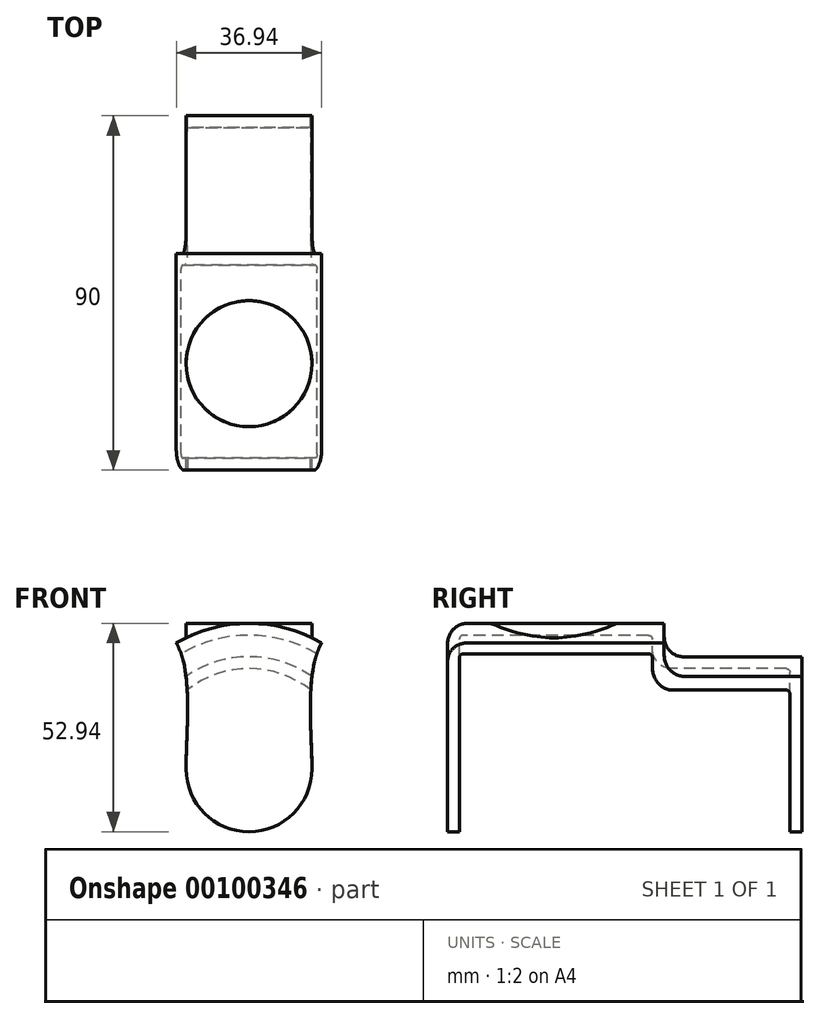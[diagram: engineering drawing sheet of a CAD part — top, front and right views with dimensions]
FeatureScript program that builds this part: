
annotation { "Feature Type Name" : "Feature", "Feature Type Description" : "" }
export const myFeature = defineFeature(function(context is Context, id is Id, definition is map)
    precondition{}
    {
        {
            var Q0;
            Q0=qCreatedBy(makeId("Front.planeOp"),FACE);
            var sketch = newSketch(context, id + "F0", { "sketchPlane" : qUnion([Q0])});
            skLineSegment(sketch, "E0.bottom", {"start": v(24, -24) * mm, "end": v(-24, -24) * mm});
            skLineSegment(sketch, "E0.top", {"start": v(24, 24) * mm, "end": v(-24, 24) * mm});
            skLineSegment(sketch, "E0.left", {"start": v(24, -24) * mm, "end": v(24, 24) * mm});
            skLineSegment(sketch, "E0.right", {"start": v(-24, -24) * mm, "end": v(-24, 24) * mm});
            skPoint(sketch, "E0.middle", {"position": v(0, 0) * mm});
            skLineSegment(sketch, "E1.bottom", {"start": v(18, -18) * mm, "end": v(-18, -18) * mm});
            skLineSegment(sketch, "E1.top", {"start": v(18, 18) * mm, "end": v(-18, 18) * mm});
            skLineSegment(sketch, "E1.left", {"start": v(18, -18) * mm, "end": v(18, 18) * mm});
            skLineSegment(sketch, "E1.right", {"start": v(-18, -18) * mm, "end": v(-18, 18) * mm});
            skLineSegment(sketch, "E2.bottom", {"start": v(18, 36.94) * mm, "end": v(-18, 36.94) * mm});
            skLineSegment(sketch, "E2.top", {"start": v(18, 72.94) * mm, "end": v(-18, 72.94) * mm});
            skLineSegment(sketch, "E2.left", {"start": v(18, 36.94) * mm, "end": v(18, 72.94) * mm});
            skLineSegment(sketch, "E2.right", {"start": v(-18, 36.94) * mm, "end": v(-18, 72.94) * mm});
            skPoint(sketch, "E2.middle", {"position": v(0, 54.94) * mm});
            skLineSegment(sketch, "E3.0", {"start": v(-12, 42.94) * mm, "end": v(-12, 66.94) * mm, "construction": true});
            skLineSegment(sketch, "E3.1", {"start": v(12, 42.94) * mm, "end": v(-12, 42.94) * mm, "construction": true});
            skLineSegment(sketch, "E3.2", {"start": v(12, 42.94) * mm, "end": v(12, 66.94) * mm, "construction": true});
            skLineSegment(sketch, "E3.3", {"start": v(12, 66.94) * mm, "end": v(-12, 66.94) * mm, "construction": true});
            skLineSegment(sketch, "E4.0", {"start": v(12, 12) * mm, "end": v(-12, 12) * mm, "construction": true});
            skLineSegment(sketch, "E4.1", {"start": v(12, -12) * mm, "end": v(12, 12) * mm, "construction": true});
            skLineSegment(sketch, "E4.2", {"start": v(12, -12) * mm, "end": v(-12, -12) * mm, "construction": true});
            skLineSegment(sketch, "E4.3", {"start": v(-12, -12) * mm, "end": v(-12, 12) * mm, "construction": true});
            skLineSegment(sketch, "E5.0", {"start": v(18, 18) * mm, "end": v(-18, 18) * mm, "construction": true});
            skLineSegment(sketch, "E5.1", {"start": v(18, -18) * mm, "end": v(18, 18) * mm, "construction": true});
            skLineSegment(sketch, "E5.2", {"start": v(18, -18) * mm, "end": v(-18, -18) * mm, "construction": true});
            skLineSegment(sketch, "E5.3", {"start": v(-18, -18) * mm, "end": v(-18, 18) * mm, "construction": true});
            skCircle(sketch, "E6", {"center": v(0, 0) * mm, "radius": 25.46 * mm, "construction": true});
            skCircle(sketch, "E7", {"center": v(0, 0) * mm, "radius": 33.94 * mm, "construction": true});
            skLineSegment(sketch, "E8", {"start": v(28.71, 17.25) * mm, "end": v(28.71, 0) * mm, "construction": true});
            skSolve(sketch);
        }
        {
            var Q0;
            Q0=qCreatedBy(makeId("Right.planeOp"),FACE);
            var sketch = newSketch(context, id + "F1", { "sketchPlane" : qUnion([Q0])});
            skLineSegment(sketch, "E9.bottom", {"start": v(-24, -24) * mm, "end": v(24, -24) * mm});
            skLineSegment(sketch, "E9.top", {"start": v(-24, 24) * mm, "end": v(24, 24) * mm});
            skLineSegment(sketch, "E9.left", {"start": v(-24, -24) * mm, "end": v(-24, 24) * mm});
            skLineSegment(sketch, "E9.right", {"start": v(24, -24) * mm, "end": v(24, 24) * mm});
            skPoint(sketch, "E9.middle", {"position": v(0, 0) * mm});
            skLineSegment(sketch, "E10.bottom", {"start": v(24, -18) * mm, "end": v(60, -18) * mm});
            skLineSegment(sketch, "E10.top", {"start": v(24, 18) * mm, "end": v(60, 18) * mm});
            skLineSegment(sketch, "E10.left", {"start": v(24, -18) * mm, "end": v(24, 18) * mm});
            skLineSegment(sketch, "E10.right", {"start": v(60, -18) * mm, "end": v(60, 18) * mm});
            skPoint(sketch, "E10.middle", {"position": v(42, 0) * mm});
            skCircle(sketch, "E11", {"center": v(0, 0) * mm, "radius": 22 * mm});
            skLineSegment(sketch, "E12.bottom", {"start": v(-18, 36.94) * mm, "end": v(18, 36.94) * mm});
            skLineSegment(sketch, "E12.top", {"start": v(-18, 72.94) * mm, "end": v(18, 72.94) * mm});
            skLineSegment(sketch, "E12.left", {"start": v(-18, 36.94) * mm, "end": v(-18, 72.94) * mm});
            skLineSegment(sketch, "E12.right", {"start": v(18, 36.94) * mm, "end": v(18, 72.94) * mm});
            skPoint(sketch, "E12.middle", {"position": v(0, 54.94) * mm});
            skSolve(sketch);
        }
        {
            var Q0;
            Q0=qCreatedBy(makeId("Front.planeOp"),FACE);
            var sketch = newSketch(context, id + "F2", { "sketchPlane" : qUnion([Q0])});
            skArc(sketch, "E13", {"start": v(0, 33.94) * mm, "mid": v(-8.94, 32.74) * mm, "end": v(-17.25, 29.23) * mm});
            skLineSegment(sketch, "E14", {"start": v(0, 0) * mm, "end": v(-18.47, 32) * mm, "construction": true});
            skArc(sketch, "E15", {"start": v(0, 16) * mm, "mid": v(-16, 0) * mm, "end": v(0, -16) * mm});
            skArc(sketch, "E16", {"start": v(0, 36.94) * mm, "mid": v(-9.56, 35.68) * mm, "end": v(-18.47, 32) * mm});
            skFitSpline(sketch, "E17", {"points": [v(-18.47, 32) * mm, v(-16, 0) * mm], "startDerivative": vector(13.12, -22.72) * mm, "endDerivative": vector(0, -27.41) * mm});
            skLineSegment(sketch, "E18", {"start": v(0, 36.94) * mm, "end": v(0, -16) * mm});
            skSolve(sketch);
        }
        {
            var Q0;
            Q0 = qSketchRegion(id + "F2", true);
            extrude(context, id + "F3", {"entities" : qUnion([Q0]), "depth" : (48 / 2 + 3) * mm, "hasSecondDirection" : true, "secondDirectionOppositeDirection" : true, "secondDirectionDepth" : (48 / 2 + 36 + 3) * mm});
        }
        {
            var Q0;
            Q0=qCreatedBy(makeId("Right.planeOp"),FACE);
            var sketch = newSketch(context, id + "F4", { "sketchPlane" : qUnion([Q0])});
            skCircle(sketch, "E19", {"center": v(0, 0) * mm, "radius": 33.94 * mm, "construction": true});
            skCircle(sketch, "E20", {"center": v(42, 0) * mm, "radius": 25.46 * mm, "construction": true});
            skLineSegment(sketch, "E21", {"start": v(-24, 33.94) * mm, "end": v(25, 33.94) * mm});
            skLineSegment(sketch, "E22", {"start": v(25, 33.94) * mm, "end": v(25, 30.46) * mm});
            skLineSegment(sketch, "E23", {"start": v(30, 25.46) * mm, "end": v(60, 25.46) * mm});
            skLineSegment(sketch, "E24", {"start": v(60, 25.46) * mm, "end": v(60, 0) * mm});
            skLineSegment(sketch, "E25", {"start": v(60, 0) * mm, "end": v(-24, 0) * mm});
            skLineSegment(sketch, "E26", {"start": v(-24, 0) * mm, "end": v(-24, 33.94) * mm});
            skLineSegment(sketch, "E27.bottom", {"start": v(63, 36.94) * mm, "end": v(28, 36.94) * mm});
            skLineSegment(sketch, "E27.top", {"start": v(63, 28.46) * mm, "end": v(33, 28.46) * mm});
            skLineSegment(sketch, "E27.left", {"start": v(63, 36.94) * mm, "end": v(63, 28.46) * mm});
            skLineSegment(sketch, "E27.right", {"start": v(28, 36.94) * mm, "end": v(28, 33.46) * mm});
            skPoint(sketch, "E28.visualSharp", {"position": v(28, 28.46) * mm});
            skArc(sketch, "E28.filletArc", {"start": v(28, 33.46) * mm, "mid": v(29.46, 29.92) * mm, "end": v(33, 28.46) * mm});
            skPoint(sketch, "E29.visualSharp", {"position": v(25, 25.46) * mm});
            skArc(sketch, "E29.filletArc", {"start": v(25, 30.46) * mm, "mid": v(26.46, 26.92) * mm, "end": v(30, 25.46) * mm});
            skSolve(sketch);
        }
        {
            var Q0;
            Q0 = qSketchRegion(id + "F4", true);
            var Q1;
            Q1=sQuery(id+"F4.wireOp",EDGE,"E25");
            revolve(context, id + "F5", {"operationType" : NewBodyOperationType.REMOVE, "entities" : qUnion([Q0]), "axis" : qUnion([Q1]), "revolveType" : RevolveType.FULL, "oppositeDirection" : true});
        }
        {
            var Q0;
            Q0=makeQuery(id+"F5.boolean.opBoolean","COPY",EDGE,{"derivedFrom":makeQuery(id+"F5.opRevolve","SWEPT_EDGE",EDGE,{"disambiguationData":[OSD([sQuery(id+"F4.wireOp",EDGE,"E27.bottom"),sQuery(id+"F4.wireOp",EDGE,"E27.right")])]})});
            var Q1;
            Q1=makeQuery(id+"F5.boolean.opBoolean","COPY",EDGE,{"derivedFrom":makeQuery(id+"F5.opRevolve","SWEPT_EDGE",EDGE,{"disambiguationData":[OSD([sQuery(id+"F4.wireOp",EDGE,"E27.top"),sQuery(id+"F4.wireOp",EDGE,"E27.left")])]})});
            var Q2;
            Q2=makeQuery(id+"F3.opExtrude","CAP_EDGE",EDGE,{"disambiguationData":[OSD([sQuery(id+"F2.wireOp",EDGE,"E16")])],"isStart":false});
            fillet(context, id + "F6", {"entities" : qUnion([Q0, Q1, Q2]), "radius" : 5 * mm, "tangentPropagation" : true, "allowEdgeOverflow" : false});
        }
        {
            var Q0;
            Q0=qCreatedBy(makeId("Top.planeOp"),FACE);
            var Q1;
            Q1=sQuery(id+"F0.wireOp",VERTEX,"E2.bottom.start");
            cPlane(context, id + "F7", {"entities" : qUnion([Q0, Q1]), "cplaneType" : CPlaneType.PLANE_POINT, "offset" : 150 * mm, "width" : 150 * mm, "height" : 150 * mm});
        }
        {
            var Q0;
            Q0=qCreatedBy(id+"F7.planeOp",FACE);
            var sketch = newSketch(context, id + "F8", { "sketchPlane" : qUnion([Q0])});
            skCircle(sketch, "E30", {"center": v(0, 0) * mm, "radius": 16 * mm});
            skLineSegment(sketch, "E31", {"start": v(0, 16) * mm, "end": v(0, -16) * mm});
            skSolve(sketch);
        }
        {
            var Q0;
            {var subQ0=sQuery(id+"F8.wireOp",EDGE,"E31");Q0=makeQuery(id+"F8.imprint","IMPRINT",FACE,{"disambiguationData":[TD([[makeQuery(id+"F8.imprint","IMPRINT",EDGE,{"derivedFrom":subQ0}),-1.0]])]});}
            var Q1;
            Q1=makeQuery(id+"F3.opExtrude","SWEPT_FACE",FACE,{"disambiguationData":[OSD([sQuery(id+"F2.wireOp",EDGE,"E16")])]});
            var Q2;
            Q2=makeQuery(id+"F3.opExtrude","SWEPT_BODY",BODY,{"disambiguationData":[OSD([sQuery(id+"F2.wireOp",EDGE,"E15"),sQuery(id+"F2.wireOp",EDGE,"E16"),sQuery(id+"F2.wireOp",EDGE,"E17"),sQuery(id+"F2.wireOp",EDGE,"E18")])]});
            extrude(context, id + "F9", {"entities" : qUnion([Q0]), "operationType" : NewBodyOperationType.ADD, "endBound" : BoundingType.UP_TO_BODY, "oppositeDirection" : true, "endBoundEntityFace" : qUnion([Q1]), "endBoundEntityBody" : qUnion([Q2]), "depth" : 25 * mm});
        }
        {
            var Q0;
            Q0=makeQuery(id+"F5.boolean.opBoolean","COPY",EDGE,{"derivedFrom":makeQuery(id+"F5.opRevolve","SWEPT_EDGE",EDGE,{"disambiguationData":[OSD([sQuery(id+"F4.wireOp",EDGE,"E23"),sQuery(id+"F4.wireOp",EDGE,"E24")])]})});
            var Q1;
            Q1=makeQuery(id+"F5.boolean.opBoolean","COPY",EDGE,{"derivedFrom":makeQuery(id+"F5.opRevolve","SWEPT_EDGE",EDGE,{"disambiguationData":[OSD([sQuery(id+"F4.wireOp",EDGE,"E21"),sQuery(id+"F4.wireOp",EDGE,"E22")])]})});
            var Q2;
            Q2=makeQuery(id+"F5.boolean.opBoolean","COPY",EDGE,{"derivedFrom":makeQuery(id+"F5.opRevolve","SWEPT_EDGE",EDGE,{"disambiguationData":[OSD([sQuery(id+"F4.wireOp",EDGE,"E21"),sQuery(id+"F4.wireOp",EDGE,"E26")])]})});
            var Q3;
            {var subQ0=sQuery(id+"F8.wireOp",EDGE,"E31");var subQ1=sQuery(id+"F8.wireOp",EDGE,"E30");Q3=makeQuery(id+"F9.opExtrude","TWEAK_EDGE",EDGE,{"derivedFrom":[makeQuery(id+"F3.opExtrude","SWEPT_FACE",FACE,{"disambiguationData":[OSD([sQuery(id+"F2.wireOp",EDGE,"E16")])]}),makeQuery(id+"F8.imprint","IMPRINT",EDGE,{"disambiguationData":[TD([[makeQuery(id+"F8.imprint","INTERSECT",VERTEX,{"disambiguationData":[OD(0.0)],"derivedFrom":[subQ1,subQ0]}),-1.0]])],"derivedFrom":subQ1})]});}
            fillet(context, id + "F10", {"entities" : qUnion([Q0, Q1, Q2, Q3]), "radius" : 1 * mm, "tangentPropagation" : true, "allowEdgeOverflow" : false});
        }
        {
            var Q0;
            Q0=makeQuery(id+"F3.opExtrude","SWEPT_BODY",BODY,{"disambiguationData":[OSD([sQuery(id+"F2.wireOp",EDGE,"E15"),sQuery(id+"F2.wireOp",EDGE,"E16"),sQuery(id+"F2.wireOp",EDGE,"E17"),sQuery(id+"F2.wireOp",EDGE,"E18")])]});
            var Q1;
            Q1=qCreatedBy(makeId("Right.planeOp"),FACE);
            mirror(context, id + "F11", {"operationType" : NewBodyOperationType.ADD, "entities" : qUnion([Q0]), "mirrorPlane" : qUnion([Q1])});
        }
    });
